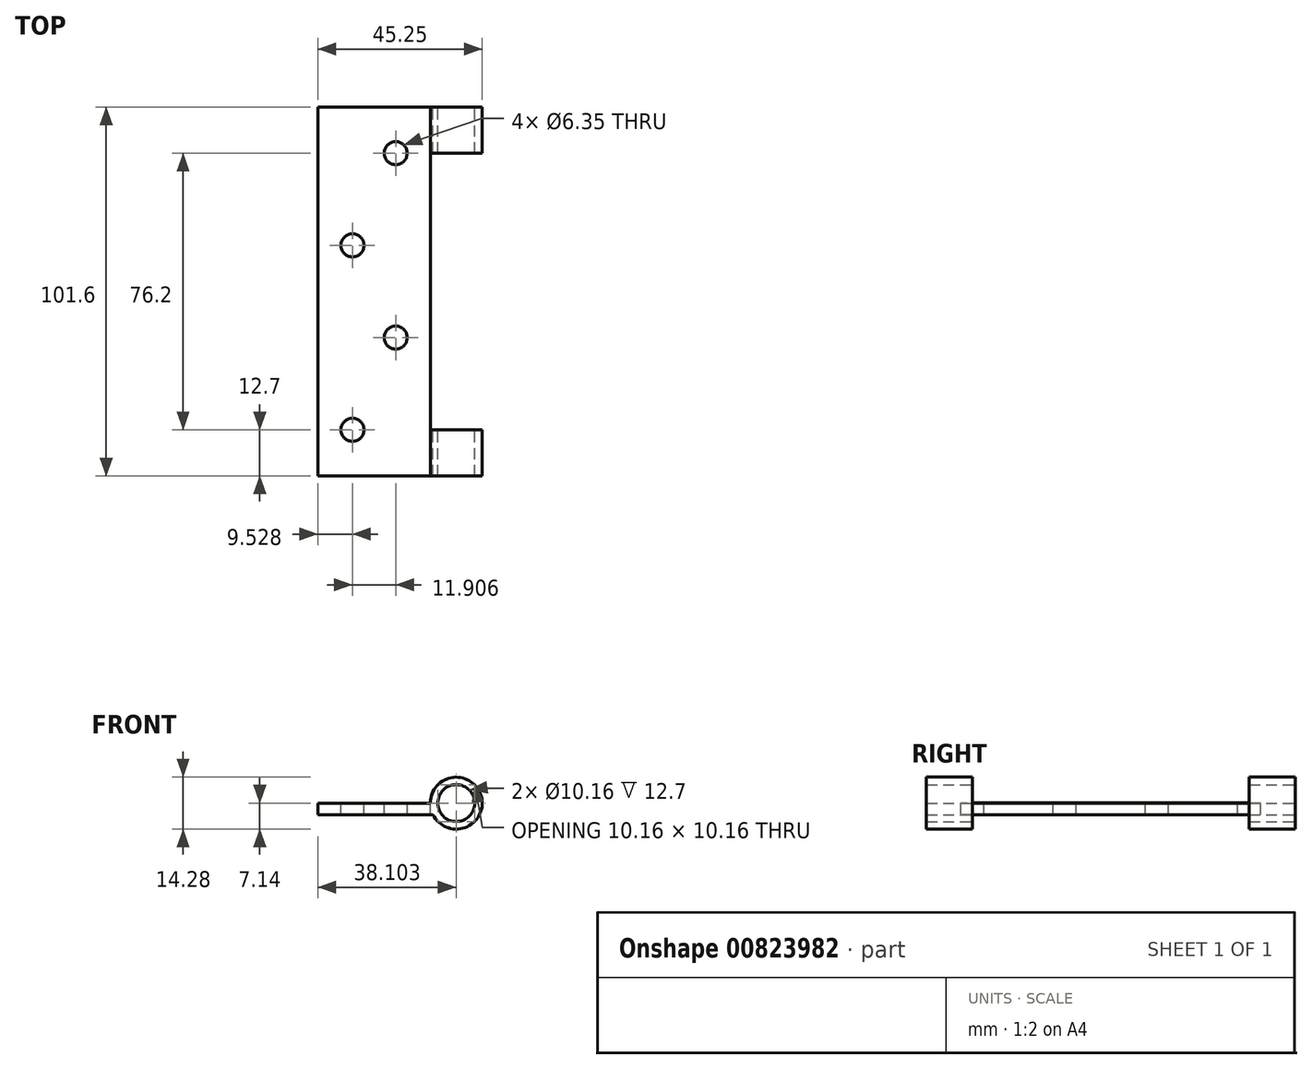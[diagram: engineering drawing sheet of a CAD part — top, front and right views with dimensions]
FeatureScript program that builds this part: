
annotation { "Feature Type Name" : "Feature", "Feature Type Description" : "" }
export const myFeature = defineFeature(function(context is Context, id is Id, definition is map)
    precondition{}
    {
        {
            var Q0;
            Q0=qCreatedBy(makeId("Front.planeOp"),FACE);
            var sketch = newSketch(context, id + "F0", { "sketchPlane" : qUnion([Q0])});
            skCircle(sketch, "E0", {"center": v(14.64, 0) * mm, "radius": 7.14 * mm});
            skCircle(sketch, "E1", {"center": v(14.64, 0) * mm, "radius": 5.08 * mm});
            skLineSegment(sketch, "E2.right", {"start": v(-23.46, 0) * mm, "end": v(-23.46, -3.17) * mm});
            skLineSegment(sketch, "E3.trimOffspring", {"start": v(7.5, 0) * mm, "end": v(-23.46, 0) * mm});
            skLineSegment(sketch, "E4", {"start": v(7.5, 0) * mm, "end": v(14.64, 0) * mm, "construction": true});
            skLineSegment(sketch, "E5", {"start": v(14.64, 0) * mm, "end": v(14.64, -3.17) * mm, "construction": true});
            skLineSegment(sketch, "E6.trimOffspring", {"start": v(8.24, -3.17) * mm, "end": v(-23.46, -3.17) * mm});
            skLineSegment(sketch, "E7", {"start": v(8.24, -3.17) * mm, "end": v(14.64, -3.17) * mm, "construction": true});
            skSolve(sketch);
        }
        {
            var Q0;
            Q0=makeQuery(id+"F0.imprint","IMPRINT",FACE,{"disambiguationData":[TD([[makeQuery(id+"F0.imprint","IMPRINT",EDGE,{"derivedFrom":sQuery(id+"F0.wireOp",EDGE,"E2.right")}),1.0]])]});
            var Q1;
            Q1=makeQuery(id+"F0.imprint","IMPRINT",FACE,{"disambiguationData":[TD([[makeQuery(id+"F0.imprint","IMPRINT",EDGE,{"derivedFrom":sQuery(id+"F0.wireOp",EDGE,"E1")}),-1.0]])]});
            extrude(context, id + "F1", {"entities" : qUnion([Q0, Q1]), "endBound" : BoundingType.SYMMETRIC, "depth" : 101.6 * mm, "offsetDistance" : 25.4 * mm});
        }
        {
            var Q0;
            Q0=qCreatedBy(makeId("Top.planeOp"),FACE);
            var sketch = newSketch(context, id + "F2", { "sketchPlane" : qUnion([Q0])});
            skLineSegment(sketch, "E8.bottom", {"start": v(22.96, 38.1) * mm, "end": v(7.5, 38.1) * mm});
            skLineSegment(sketch, "E8.top", {"start": v(22.96, -38.1) * mm, "end": v(7.5, -38.1) * mm});
            skLineSegment(sketch, "E8.left", {"start": v(22.96, 38.1) * mm, "end": v(22.96, -38.1) * mm});
            skLineSegment(sketch, "E8.right", {"start": v(7.5, 38.1) * mm, "end": v(7.5, -38.1) * mm});
            skSolve(sketch);
        }
        {
            var Q0;
            Q0 = qSketchRegion(id + "F2", true);
            extrude(context, id + "F3", {"entities" : qUnion([Q0]), "operationType" : NewBodyOperationType.REMOVE, "endBound" : BoundingType.SYMMETRIC, "oppositeDirection" : true, "depth" : 25.4 * mm, "offsetDistance" : 25.4 * mm});
        }
        {
            var Q0;
            Q0=makeQuery(id+"F1.opExtrude","SWEPT_FACE",FACE,{"disambiguationData":[OSD([sQuery(id+"F0.wireOp",EDGE,"E3.trimOffspring")])]});
            var sketch = newSketch(context, id + "F4", { "sketchPlane" : qUnion([Q0])});
            skCircle(sketch, "E9", {"center": v(-2.03, 38.1) * mm, "radius": 3.18 * mm});
            skCircle(sketch, "E10", {"center": v(-2.03, -12.7) * mm, "radius": 3.18 * mm});
            skCircle(sketch, "E11", {"center": v(-13.93, 12.7) * mm, "radius": 3.18 * mm});
            skCircle(sketch, "E12", {"center": v(-13.93, -38.1) * mm, "radius": 3.18 * mm});
            skSolve(sketch);
        }
        {
            var Q0;
            Q0=sQuery(id+"F4.wireOp",VERTEX,"E9.center");
            var Q1;
            Q1=sQuery(id+"F4.wireOp",VERTEX,"E11.center");
            var Q2;
            Q2=sQuery(id+"F4.wireOp",VERTEX,"E10.center");
            var Q3;
            Q3=sQuery(id+"F4.wireOp",VERTEX,"E12.center");
            var Q4;
            Q4=makeQuery(id+"F1.opExtrude","SWEPT_BODY",BODY,{"disambiguationData":[OSD([sQuery(id+"F0.wireOp",EDGE,"E0"),sQuery(id+"F0.wireOp",EDGE,"E1"),sQuery(id+"F0.wireOp",EDGE,"E2.right"),sQuery(id+"F0.wireOp",EDGE,"E3.trimOffspring"),sQuery(id+"F0.wireOp",EDGE,"E6.trimOffspring")])]});
            hole(context, id + "F5", {"style" : HoleStyle.SIMPLE, "endStyle" : HoleEndStyle.THROUGH, "holeDiameter" : 6.35 * mm, "majorDiameter" : 6.35 * mm, "isTappedThrough" : true, "tappedDepth" : 12.7 * mm, "tapClearance" : 3, "locations" : qUnion([Q0, Q1, Q2, Q3]), "scope" : qUnion([Q4])});
        }
    });
